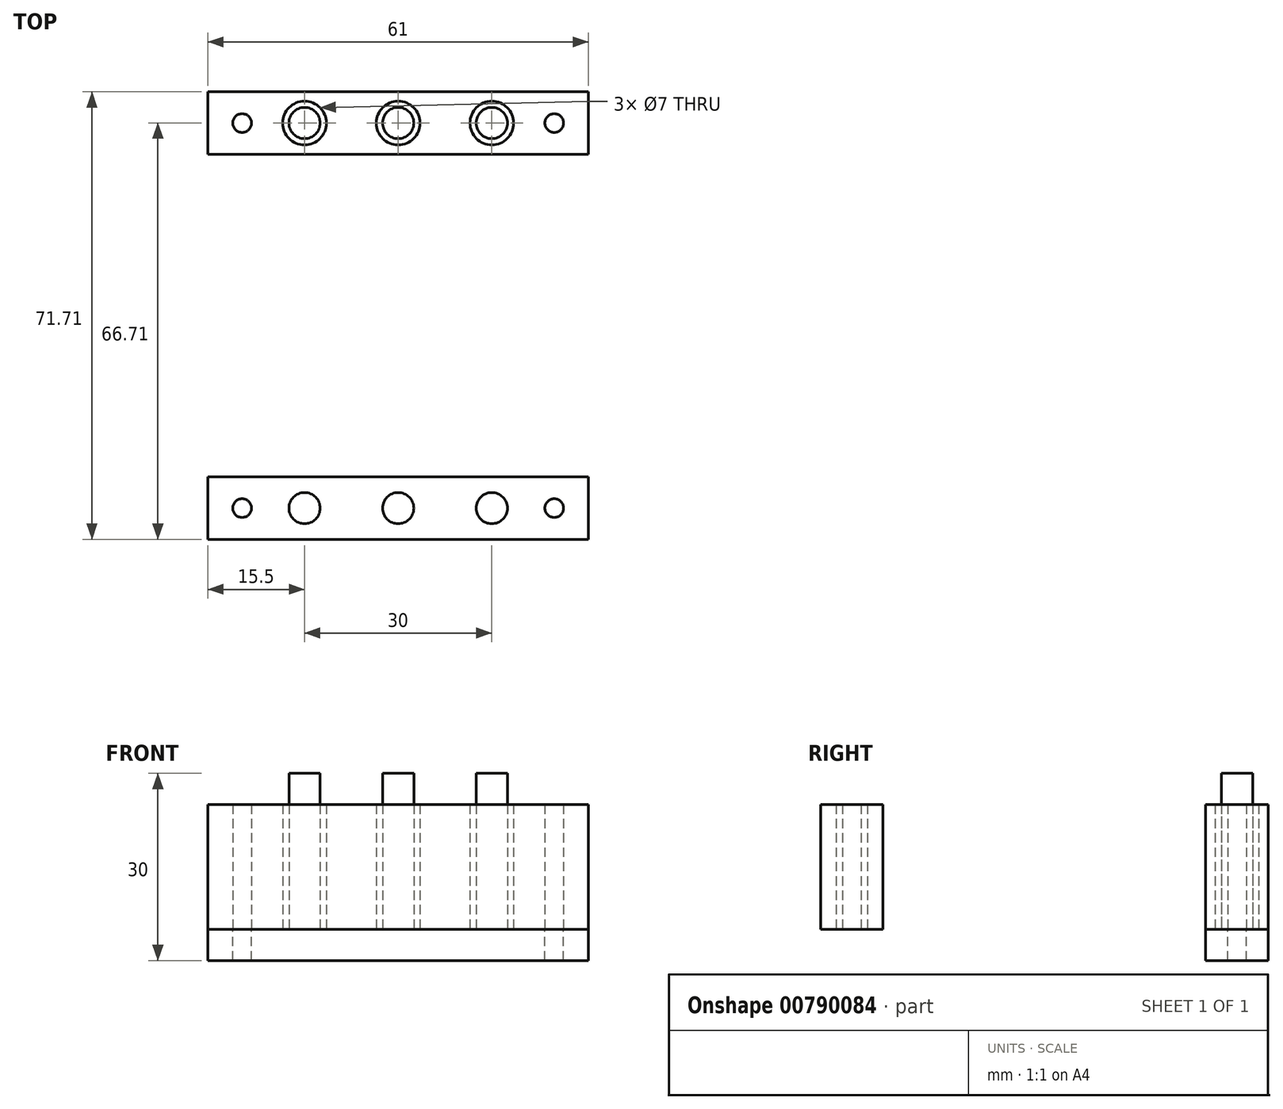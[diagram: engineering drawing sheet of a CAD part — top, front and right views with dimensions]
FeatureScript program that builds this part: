
annotation { "Feature Type Name" : "Feature", "Feature Type Description" : "" }
export const myFeature = defineFeature(function(context is Context, id is Id, definition is map)
    precondition{}
    {
        {
            var Q0;
            Q0=qCreatedBy(makeId("Top.planeOp"),FACE);
            var sketch = newSketch(context, id + "F0", { "sketchPlane" : qUnion([Q0])});
            skLineSegment(sketch, "E0.bottom", {"start": v(30.5, 5) * mm, "end": v(-30.5, 5) * mm});
            skLineSegment(sketch, "E0.top", {"start": v(30.5, -5) * mm, "end": v(-30.5, -5) * mm});
            skLineSegment(sketch, "E0.left", {"start": v(30.5, 5) * mm, "end": v(30.5, -5) * mm});
            skLineSegment(sketch, "E0.right", {"start": v(-30.5, 5) * mm, "end": v(-30.5, -5) * mm});
            skPoint(sketch, "E0.middle", {"position": v(0, 0) * mm});
            skCircle(sketch, "E1", {"center": v(0, 0) * mm, "radius": 3.5 * mm});
            skCircle(sketch, "E2", {"center": v(0, 0) * mm, "radius": 2.5 * mm});
            skCircle(sketch, "E3", {"center": v(15, 0) * mm, "radius": 2.5 * mm});
            skCircle(sketch, "E4", {"center": v(15, 0) * mm, "radius": 3.5 * mm});
            skCircle(sketch, "E5", {"center": v(25, 0) * mm, "radius": 1.5 * mm});
            skCircle(sketch, "E6.MirrorC", {"center": v(-15, 0) * mm, "radius": 2.5 * mm});
            skCircle(sketch, "E7.MirrorC", {"center": v(-15, 0) * mm, "radius": 3.5 * mm});
            skCircle(sketch, "E8.MirrorC", {"center": v(-25, 0) * mm, "radius": 1.5 * mm});
            skSolve(sketch);
        }
        {
            var Q0;
            Q0=makeQuery(id+"F0.imprint","IMPRINT",FACE,{"disambiguationData":[TD([[makeQuery(id+"F0.imprint","IMPRINT",EDGE,{"derivedFrom":sQuery(id+"F0.wireOp",EDGE,"E0.bottom")}),1.0]])]});
            extrude(context, id + "F1", {"entities" : qUnion([Q0]), "depth" : 20 * mm, "offsetDistance" : 25 * mm});
        }
        {
            var Q0;
            Q0=makeQuery(id+"F1.opExtrude","CAP_FACE",FACE,{"disambiguationData":[OSD([sQuery(id+"F0.wireOp",EDGE,"E0.bottom"),sQuery(id+"F0.wireOp",EDGE,"E0.top"),sQuery(id+"F0.wireOp",EDGE,"E0.left"),sQuery(id+"F0.wireOp",EDGE,"E0.right"),sQuery(id+"F0.wireOp",EDGE,"E1"),sQuery(id+"F0.wireOp",EDGE,"E4"),sQuery(id+"F0.wireOp",EDGE,"E5"),sQuery(id+"F0.wireOp",EDGE,"E7.MirrorC"),sQuery(id+"F0.wireOp",EDGE,"E8.MirrorC")])],"isStart":true});
            var sketch = newSketch(context, id + "F2", { "sketchPlane" : qUnion([Q0])});
            skLineSegment(sketch, "E9.0.0", {"start": v(30.5, 5) * mm, "end": v(-30.5, 5) * mm});
            skLineSegment(sketch, "E9.0.1", {"start": v(-30.5, 5) * mm, "end": v(-30.5, -5) * mm});
            skLineSegment(sketch, "E9.0.2", {"start": v(-30.5, -5) * mm, "end": v(30.5, -5) * mm});
            skLineSegment(sketch, "E9.0.3", {"start": v(30.5, -5) * mm, "end": v(30.5, 5) * mm});
            skCircle(sketch, "E10.0.0", {"center": v(-15, 0) * mm, "radius": 2.5 * mm});
            skCircle(sketch, "E11.0.0", {"center": v(0, 0) * mm, "radius": 2.5 * mm});
            skCircle(sketch, "E12.0.0", {"center": v(15, 0) * mm, "radius": 2.5 * mm});
            skSolve(sketch);
        }
        {
            var Q0;
            Q0=makeQuery(id+"F2.imprint","IMPRINT",FACE,{"disambiguationData":[TD([[makeQuery(id+"F2.imprint","IMPRINT",EDGE,{"derivedFrom":sQuery(id+"F2.wireOp",EDGE,"E9.0.0")}),1.0]])]});
            var Q1;
            Q1=makeQuery(id+"F2.imprint","IMPRINT",FACE,{"disambiguationData":[TD([[makeQuery(id+"F2.imprint","IMPRINT",EDGE,{"derivedFrom":sQuery(id+"F2.wireOp",EDGE,"E10.0.0")}),-1.0]])]});
            var Q2;
            Q2=makeQuery(id+"F2.imprint","IMPRINT",FACE,{"disambiguationData":[TD([[makeQuery(id+"F2.imprint","IMPRINT",EDGE,{"derivedFrom":sQuery(id+"F2.wireOp",EDGE,"E11.0.0")}),-1.0]])]});
            var Q3;
            Q3=makeQuery(id+"F2.imprint","IMPRINT",FACE,{"disambiguationData":[TD([[makeQuery(id+"F2.imprint","IMPRINT",EDGE,{"derivedFrom":sQuery(id+"F2.wireOp",EDGE,"E12.0.0")}),-1.0]])]});
            extrude(context, id + "F3", {"entities" : qUnion([Q0, Q1, Q2, Q3]), "depth" : 5 * mm, "offsetDistance" : 25 * mm});
        }
        {
            var Q0;
            Q0=makeQuery(id+"F2.imprint","IMPRINT",FACE,{"disambiguationData":[TD([[makeQuery(id+"F2.imprint","IMPRINT",EDGE,{"derivedFrom":sQuery(id+"F2.wireOp",EDGE,"E12.0.0")}),1.0]])]});
            var Q1;
            Q1=makeQuery(id+"F2.imprint","IMPRINT",FACE,{"disambiguationData":[TD([[makeQuery(id+"F2.imprint","IMPRINT",EDGE,{"derivedFrom":sQuery(id+"F2.wireOp",EDGE,"E11.0.0")}),1.0]])]});
            var Q2;
            Q2=makeQuery(id+"F2.imprint","IMPRINT",FACE,{"disambiguationData":[TD([[makeQuery(id+"F2.imprint","IMPRINT",EDGE,{"derivedFrom":sQuery(id+"F2.wireOp",EDGE,"E10.0.0")}),1.0]])]});
            extrude(context, id + "F4", {"entities" : qUnion([Q0, Q1, Q2]), "operationType" : NewBodyOperationType.ADD, "oppositeDirection" : true, "depth" : 25 * mm, "offsetDistance" : 25 * mm, "hasSecondDirection" : true, "secondDirectionOppositeDirection" : false, "secondDirectionDepth" : 5 * mm});
        }
        {
            var Q0;
            Q0=qCreatedBy(makeId("Top.planeOp"),FACE);
            var sketch = newSketch(context, id + "F5", { "sketchPlane" : qUnion([Q0])});
            skLineSegment(sketch, "E13.bottom", {"start": v(30.5, -56.71) * mm, "end": v(-30.5, -56.71) * mm});
            skLineSegment(sketch, "E13.top", {"start": v(30.5, -66.71) * mm, "end": v(-30.5, -66.71) * mm});
            skLineSegment(sketch, "E13.left", {"start": v(30.5, -56.71) * mm, "end": v(30.5, -66.71) * mm});
            skLineSegment(sketch, "E13.right", {"start": v(-30.5, -56.71) * mm, "end": v(-30.5, -66.71) * mm});
            skPoint(sketch, "E13.middle", {"position": v(0, -61.71) * mm});
            skCircle(sketch, "E14", {"center": v(0, -61.71) * mm, "radius": 2.5 * mm});
            skCircle(sketch, "E15", {"center": v(0, -61.71) * mm, "radius": 1.5 * mm});
            skCircle(sketch, "E16", {"center": v(15, -61.71) * mm, "radius": 1.5 * mm});
            skCircle(sketch, "E17", {"center": v(15, -61.71) * mm, "radius": 2.5 * mm});
            skCircle(sketch, "E18", {"center": v(25, -61.71) * mm, "radius": 1.5 * mm});
            skLineSegment(sketch, "E19", {"start": v(-30.5, -61.71) * mm, "end": v(30.5, -61.71) * mm, "construction": true});
            skCircle(sketch, "E20.MirrorC", {"center": v(-15, -61.71) * mm, "radius": 2.5 * mm});
            skCircle(sketch, "E21.MirrorC", {"center": v(-15, -61.71) * mm, "radius": 1.5 * mm});
            skCircle(sketch, "E22.MirrorC", {"center": v(-25, -61.71) * mm, "radius": 1.5 * mm});
            skSolve(sketch);
        }
        {
            var Q0;
            Q0=makeQuery(id+"F5.imprint","IMPRINT",FACE,{"disambiguationData":[TD([[makeQuery(id+"F5.imprint","IMPRINT",EDGE,{"derivedFrom":sQuery(id+"F5.wireOp",EDGE,"E13.bottom")}),1.0]])]});
            extrude(context, id + "F6", {"entities" : qUnion([Q0]), "depth" : 20 * mm, "offsetDistance" : 25 * mm});
        }
    });
